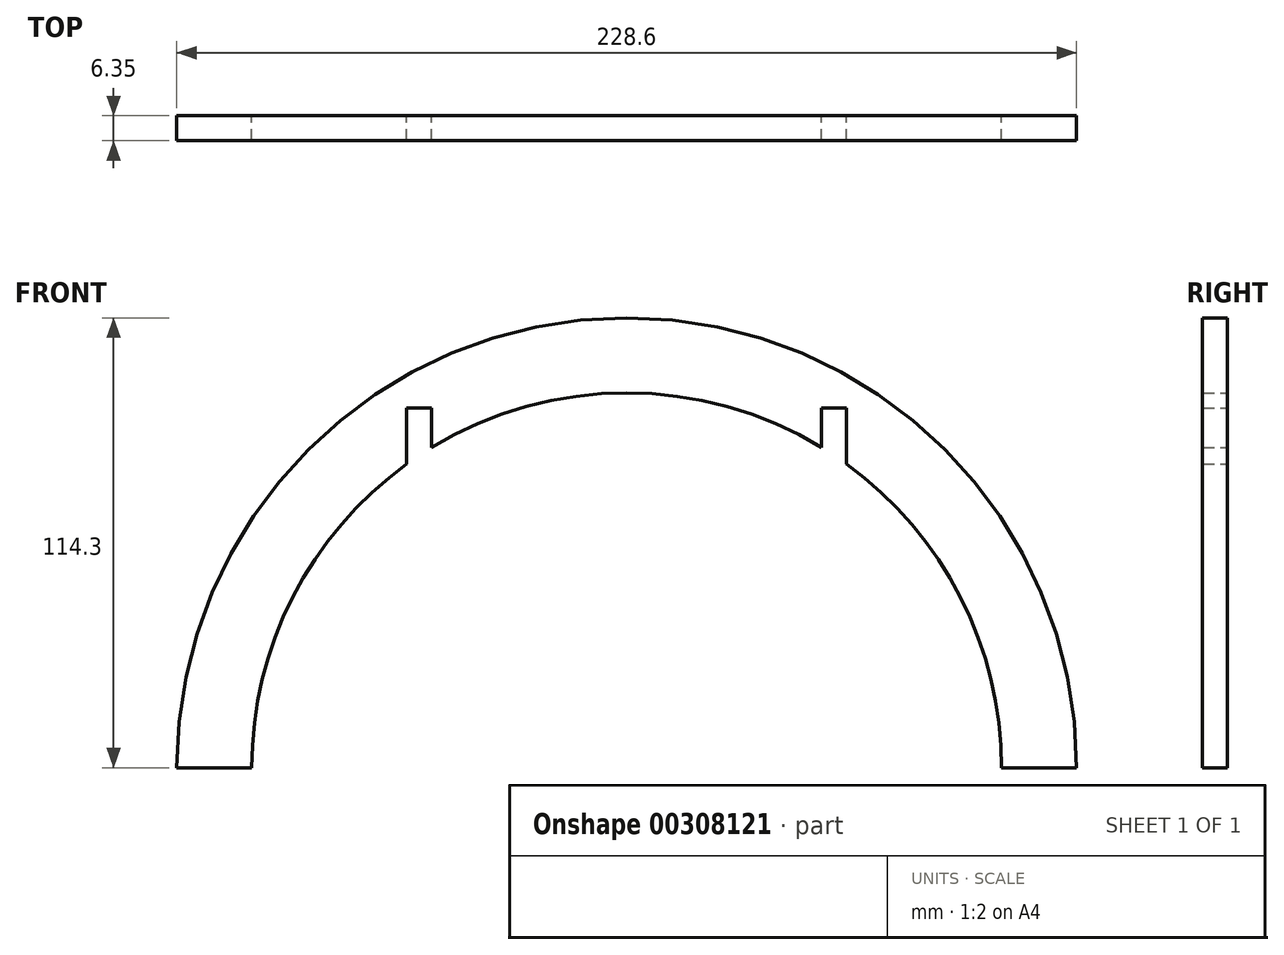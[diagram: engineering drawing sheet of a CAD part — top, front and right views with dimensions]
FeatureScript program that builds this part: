
annotation { "Feature Type Name" : "Feature", "Feature Type Description" : "" }
export const myFeature = defineFeature(function(context is Context, id is Id, definition is map)
    precondition{}
    {
        {
            var Q0;
            Q0=qCreatedBy(makeId("Front.planeOp"),FACE);
            var sketch = newSketch(context, id + "F0", { "sketchPlane" : qUnion([Q0])});
            skArc(sketch, "E0", {"start": v(114.3, 0) * mm, "mid": v(0, 114.3) * mm, "end": v(-114.3, 0) * mm});
            skPoint(sketch, "E1.orphan", {"position": v(-136.45, 0) * mm});
            skLineSegment(sketch, "E2", {"start": v(-114.3, 0) * mm, "end": v(-95.25, 0) * mm});
            skLineSegment(sketch, "E3.MirrorCS", {"start": v(114.3, 0) * mm, "end": v(95.25, 0) * mm});
            skArc(sketch, "E4", {"start": v(95.25, 0) * mm, "mid": v(0, 95.25) * mm, "end": v(-95.25, 0) * mm});
            skSolve(sketch);
        }
        {
            var Q0;
            Q0 = qSketchRegion(id + "F0", true);
            extrude(context, id + "F1", {"entities" : qUnion([Q0]), "depth" : 6.35 * mm});
        }
        {
            var Q0;
            Q0=qCreatedBy(makeId("Top.planeOp"),FACE);
            cPlane(context, id + "F2", {"entities" : qUnion([Q0]), "cplaneType" : CPlaneType.OFFSET, "offset" : 60.96 * mm, "width" : 152.4 * mm, "height" : 152.4 * mm});
        }
        {
            var Q0;
            Q0=qCreatedBy(id+"F2.planeOp",FACE);
            var sketch = newSketch(context, id + "F3", { "sketchPlane" : qUnion([Q0])});
            skLineSegment(sketch, "E5.bottom", {"start": v(-55.88, -6.35) * mm, "end": v(-49.53, -6.35) * mm});
            skLineSegment(sketch, "E5.top", {"start": v(-55.88, 0) * mm, "end": v(-49.53, 0) * mm});
            skLineSegment(sketch, "E5.left", {"start": v(-55.88, -6.35) * mm, "end": v(-55.88, 0) * mm});
            skLineSegment(sketch, "E5.right", {"start": v(-49.53, -6.35) * mm, "end": v(-49.53, 0) * mm});
            skLineSegment(sketch, "E6.MirrorCS", {"start": v(55.88, -6.35) * mm, "end": v(49.53, -6.35) * mm});
            skLineSegment(sketch, "E7.MirrorCS", {"start": v(55.88, -6.35) * mm, "end": v(55.88, 0) * mm});
            skLineSegment(sketch, "E8.MirrorCS", {"start": v(49.53, -6.35) * mm, "end": v(49.53, 0) * mm});
            skLineSegment(sketch, "E9.MirrorCS", {"start": v(55.88, 0) * mm, "end": v(49.53, 0) * mm});
            skSolve(sketch);
        }
        {
            var Q0;
            Q0 = qSketchRegion(id + "F3", true);
            extrude(context, id + "F4", {"entities" : qUnion([Q0]), "operationType" : NewBodyOperationType.REMOVE, "depth" : 30.48 * mm});
        }
    });
